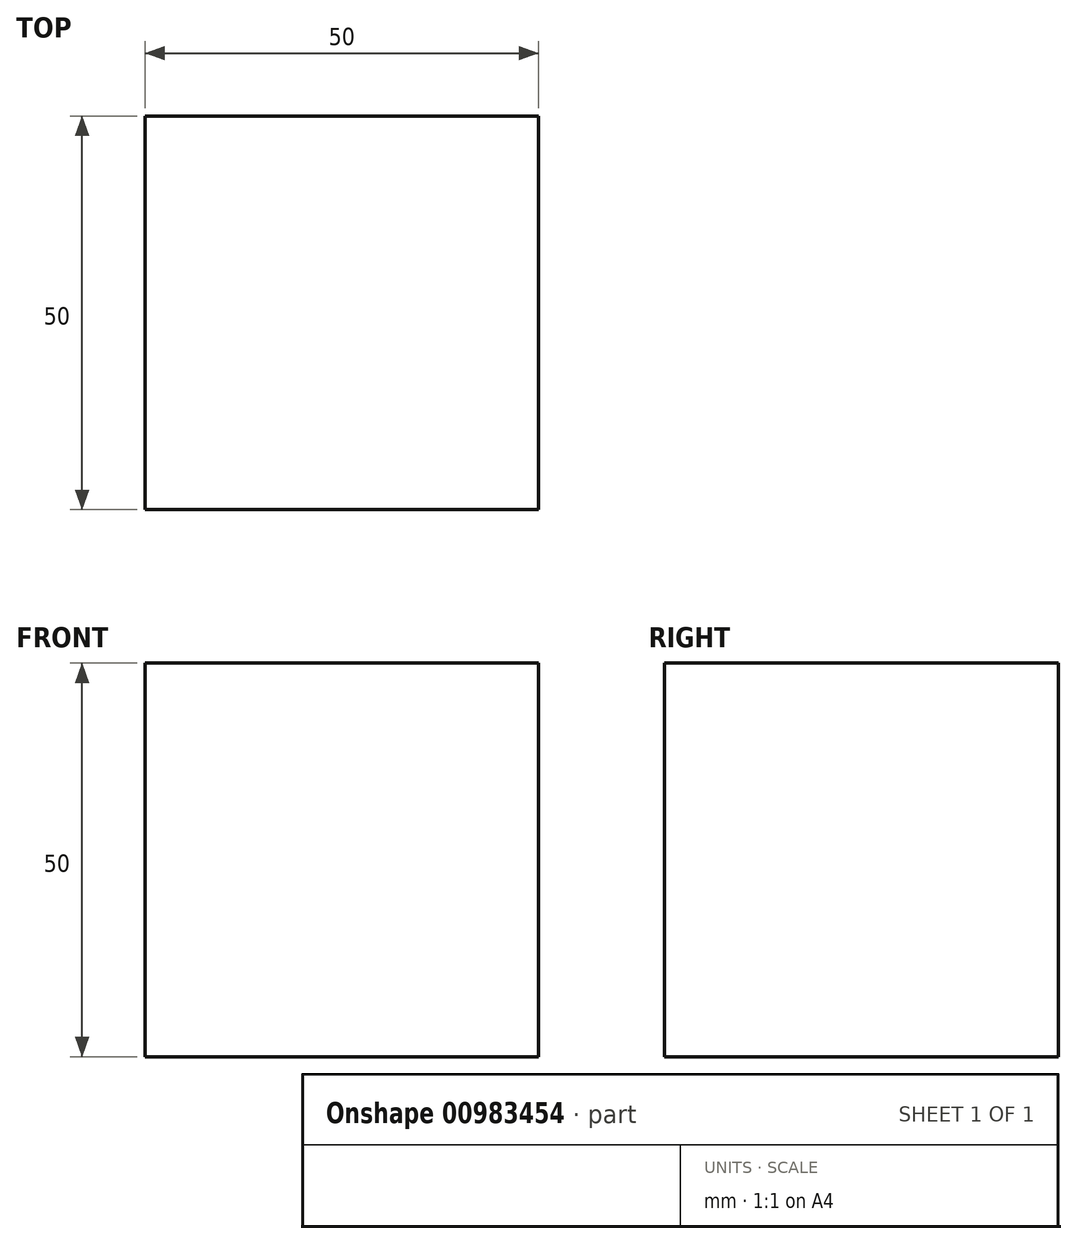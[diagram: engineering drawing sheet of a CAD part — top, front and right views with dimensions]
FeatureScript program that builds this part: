
annotation { "Feature Type Name" : "Feature", "Feature Type Description" : "" }
export const myFeature = defineFeature(function(context is Context, id is Id, definition is map)
    precondition{}
    {
        {
            var Q0;
            Q0=qCreatedBy(makeId("Front.planeOp"),FACE);
            var sketch = newSketch(context, id + "F0", { "sketchPlane" : qUnion([Q0])});
            skLineSegment(sketch, "E0.bottom", {"start": v(1.78, -5.77) * mm, "end": v(51.78, -5.77) * mm});
            skLineSegment(sketch, "E0.top", {"start": v(1.78, -55.77) * mm, "end": v(51.78, -55.77) * mm});
            skLineSegment(sketch, "E0.left", {"start": v(1.78, -5.77) * mm, "end": v(1.78, -55.77) * mm});
            skLineSegment(sketch, "E0.right", {"start": v(51.78, -5.77) * mm, "end": v(51.78, -55.77) * mm});
            skSolve(sketch);
        }
        {
            var Q0;
            Q0 = qSketchRegion(id + "F0", true);
            extrude(context, id + "F1", {"entities" : qUnion([Q0]), "depth" : 50 * mm, "offsetDistance" : 25 * mm});
        }
    });
